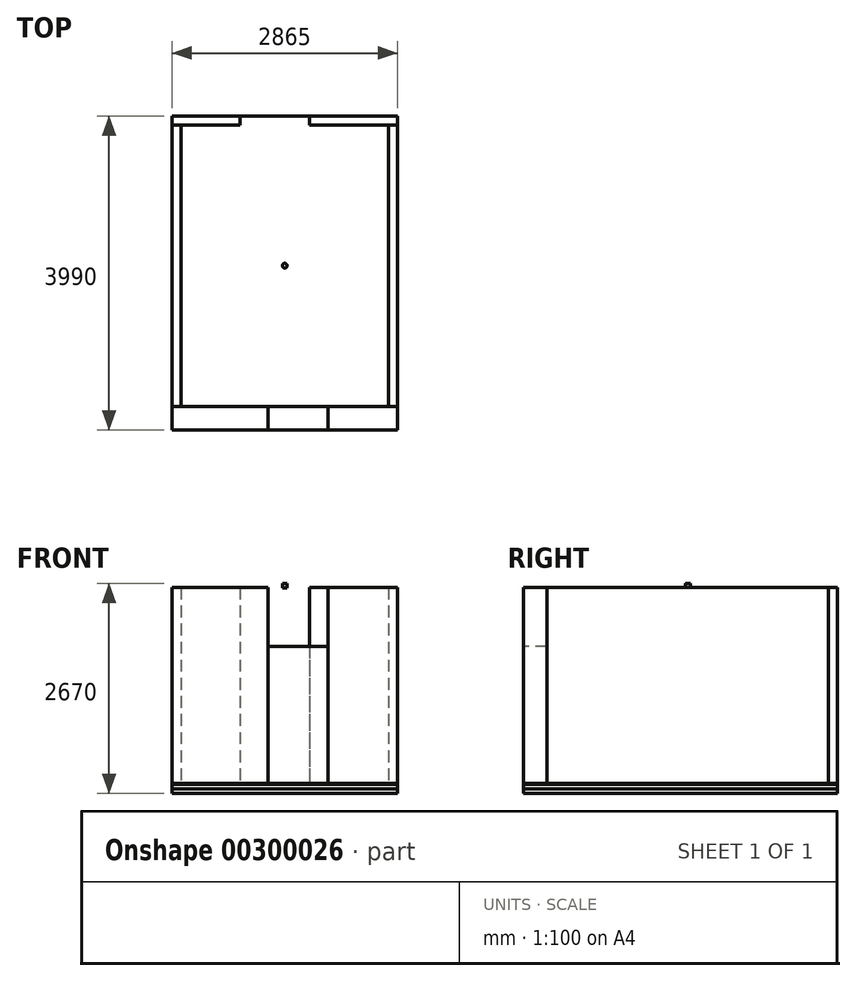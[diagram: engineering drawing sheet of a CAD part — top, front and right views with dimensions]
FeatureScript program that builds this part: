
annotation { "Feature Type Name" : "Feature", "Feature Type Description" : "" }
export const myFeature = defineFeature(function(context is Context, id is Id, definition is map)
    precondition{}
    {
        {
            var Q0;
            Q0=qCreatedBy(makeId("Top.planeOp"),FACE);
            var sketch = newSketch(context, id + "F0", { "sketchPlane" : qUnion([Q0])});
            skLineSegment(sketch, "E0.bottom", {"start": v(1317.5, -1787.5) * mm, "end": v(-1317.5, -1787.5) * mm, "construction": true});
            skLineSegment(sketch, "E0.top", {"start": v(1317.5, 1787.5) * mm, "end": v(-1317.5, 1787.5) * mm, "construction": true});
            skLineSegment(sketch, "E0.left", {"start": v(1317.5, -1787.5) * mm, "end": v(1317.5, 1787.5) * mm, "construction": true});
            skLineSegment(sketch, "E0.right", {"start": v(-1317.5, -1787.5) * mm, "end": v(-1317.5, 1787.5) * mm, "construction": true});
            skPoint(sketch, "E0.middle", {"position": v(0, 0) * mm});
            skLineSegment(sketch, "E1.bottom", {"start": v(-1317.5, 1787.5) * mm, "end": v(-1432.5, 1787.5) * mm});
            skLineSegment(sketch, "E1.top", {"start": v(-1317.5, -1787.5) * mm, "end": v(-1432.5, -1787.5) * mm});
            skLineSegment(sketch, "E1.left", {"start": v(-1317.5, 1787.5) * mm, "end": v(-1317.5, -1787.5) * mm});
            skLineSegment(sketch, "E1.right", {"start": v(-1432.5, 1787.5) * mm, "end": v(-1432.5, -1787.5) * mm});
            skLineSegment(sketch, "E2.bottom", {"start": v(1317.5, -1787.5) * mm, "end": v(1432.5, -1787.5) * mm});
            skLineSegment(sketch, "E2.top", {"start": v(1317.5, 1787.5) * mm, "end": v(1432.5, 1787.5) * mm});
            skLineSegment(sketch, "E2.left", {"start": v(1317.5, -1787.5) * mm, "end": v(1317.5, 1787.5) * mm});
            skLineSegment(sketch, "E2.right", {"start": v(1432.5, -1787.5) * mm, "end": v(1432.5, 1787.5) * mm});
            skLineSegment(sketch, "E3.bottom", {"start": v(-1432.5, -1787.5) * mm, "end": v(-212.5, -1787.5) * mm});
            skLineSegment(sketch, "E3.top", {"start": v(-1432.5, -2087.5) * mm, "end": v(-212.5, -2087.5) * mm});
            skLineSegment(sketch, "E3.left", {"start": v(-1432.5, -1787.5) * mm, "end": v(-1432.5, -2087.5) * mm});
            skLineSegment(sketch, "E3.right", {"start": v(-212.5, -1787.5) * mm, "end": v(-212.5, -2087.5) * mm});
            skLineSegment(sketch, "E4.bottom", {"start": v(1432.5, -1787.5) * mm, "end": v(547.5, -1787.5) * mm});
            skLineSegment(sketch, "E4.top", {"start": v(1432.5, -2087.5) * mm, "end": v(547.5, -2087.5) * mm});
            skLineSegment(sketch, "E4.left", {"start": v(1432.5, -1787.5) * mm, "end": v(1432.5, -2087.5) * mm});
            skLineSegment(sketch, "E4.right", {"start": v(547.5, -1787.5) * mm, "end": v(547.5, -2087.5) * mm});
            skLineSegment(sketch, "E5.bottom", {"start": v(-1432.5, 1787.5) * mm, "end": v(-567.5, 1787.5) * mm});
            skLineSegment(sketch, "E5.top", {"start": v(-1432.5, 1902.5) * mm, "end": v(-567.5, 1902.5) * mm});
            skLineSegment(sketch, "E5.left", {"start": v(-1432.5, 1787.5) * mm, "end": v(-1432.5, 1902.5) * mm});
            skLineSegment(sketch, "E5.right", {"start": v(-567.5, 1787.5) * mm, "end": v(-567.5, 1902.5) * mm});
            skLineSegment(sketch, "E6.bottom", {"start": v(1432.5, 1787.5) * mm, "end": v(317.5, 1787.5) * mm});
            skLineSegment(sketch, "E6.top", {"start": v(1432.5, 1902.5) * mm, "end": v(317.5, 1902.5) * mm});
            skLineSegment(sketch, "E6.left", {"start": v(1432.5, 1787.5) * mm, "end": v(1432.5, 1902.5) * mm});
            skLineSegment(sketch, "E6.right", {"start": v(317.5, 1787.5) * mm, "end": v(317.5, 1902.5) * mm});
            skLineSegment(sketch, "E7.bottom", {"start": v(-212.5, -1787.5) * mm, "end": v(547.5, -1787.5) * mm});
            skLineSegment(sketch, "E7.top", {"start": v(-212.5, -2087.5) * mm, "end": v(547.5, -2087.5) * mm});
            skSolve(sketch);
        }
        {
            var Q0;
            Q0=qCreatedBy(makeId("Top.planeOp"),FACE);
            var sketch = newSketch(context, id + "F1", { "sketchPlane" : qUnion([Q0])});
            skLineSegment(sketch, "E8.bottom", {"start": v(-1432.5, 1902.5) * mm, "end": v(1432.5, 1902.5) * mm});
            skLineSegment(sketch, "E8.top", {"start": v(-1432.5, -2087.5) * mm, "end": v(1432.5, -2087.5) * mm});
            skLineSegment(sketch, "E8.left", {"start": v(-1432.5, 1902.5) * mm, "end": v(-1432.5, -2087.5) * mm});
            skLineSegment(sketch, "E8.right", {"start": v(1432.5, 1902.5) * mm, "end": v(1432.5, -2087.5) * mm});
            skSolve(sketch);
        }
        {
            var Q0;
            Q0 = qSketchRegion(id + "F1", true);
            extrude(context, id + "F2", {"entities" : qUnion([Q0]), "oppositeDirection" : true, "depth" : 15 * mm});
        }
        {
            var Q0;
            Q0=makeQuery(id+"F2.opExtrude","CAP_FACE",FACE,{"disambiguationData":[OSD([sQuery(id+"F1.wireOp",EDGE,"E8.bottom"),sQuery(id+"F1.wireOp",EDGE,"E8.top"),sQuery(id+"F1.wireOp",EDGE,"E8.left"),sQuery(id+"F1.wireOp",EDGE,"E8.right")])],"isStart":false});
            var sketch = newSketch(context, id + "F3", { "sketchPlane" : qUnion([Q0])});
            skLineSegment(sketch, "E9.bottom", {"start": v(1432.5, -1902.5) * mm, "end": v(-1432.5, -1902.5) * mm});
            skLineSegment(sketch, "E9.top", {"start": v(1432.5, 2087.5) * mm, "end": v(-1432.5, 2087.5) * mm});
            skLineSegment(sketch, "E9.left", {"start": v(1432.5, -1902.5) * mm, "end": v(1432.5, 2087.5) * mm});
            skLineSegment(sketch, "E9.right", {"start": v(-1432.5, -1902.5) * mm, "end": v(-1432.5, 2087.5) * mm});
            skSolve(sketch);
        }
        {
            var Q0;
            Q0 = qSketchRegion(id + "F3", true);
            extrude(context, id + "F4", {"entities" : qUnion([Q0]), "depth" : 55 * mm});
        }
        {
            var Q0;
            Q0=makeQuery(id+"F4.opExtrude","CAP_FACE",FACE,{"disambiguationData":[OSD([sQuery(id+"F3.wireOp",EDGE,"E9.bottom"),sQuery(id+"F3.wireOp",EDGE,"E9.top"),sQuery(id+"F3.wireOp",EDGE,"E9.left"),sQuery(id+"F3.wireOp",EDGE,"E9.right")])],"isStart":false});
            var sketch = newSketch(context, id + "F5", { "sketchPlane" : qUnion([Q0])});
            skLineSegment(sketch, "E10.bottom", {"start": v(1432.5, -1902.5) * mm, "end": v(-1432.5, -1902.5) * mm});
            skLineSegment(sketch, "E10.top", {"start": v(1432.5, 2087.5) * mm, "end": v(-1432.5, 2087.5) * mm});
            skLineSegment(sketch, "E10.left", {"start": v(1432.5, -1902.5) * mm, "end": v(1432.5, 2087.5) * mm});
            skLineSegment(sketch, "E10.right", {"start": v(-1432.5, -1902.5) * mm, "end": v(-1432.5, 2087.5) * mm});
            skSolve(sketch);
        }
        {
            var Q0;
            Q0 = qSketchRegion(id + "F5", true);
            extrude(context, id + "F6", {"entities" : qUnion([Q0]), "depth" : 60 * mm});
        }
        {
            assignVariable(context, id + "F7", {"name" : "Wandhoehe", "anyValue" : 2490});
        }
        {
            assignVariable(context, id + "F8", {"name" : "BRHKeller", "anyValue" : 1740});
        }
        {
            var Q0;
            {var subQ0=sQuery(id+"F0.wireOp",EDGE,"E1.left");Q0=makeQuery(id+"F0.imprint","IMPRINT",FACE,{"disambiguationData":[TD([[makeQuery(id+"F0.imprint","IMPRINT",EDGE,{"derivedFrom":subQ0}),-1.0]])]});}
            var Q1;
            {var subQ0=sQuery(id+"F0.wireOp",EDGE,"E2.left");Q1=makeQuery(id+"F0.imprint","IMPRINT",FACE,{"disambiguationData":[TD([[makeQuery(id+"F0.imprint","IMPRINT",EDGE,{"derivedFrom":subQ0}),-1.0]])]});}
            extrude(context, id + "F9", {"entities" : qUnion([Q0, Q1]), "depth" : (getVariable(context, 'Wandhoehe')) * mm});
        }
        {
            var Q0;
            Q0=makeQuery(id+"F0.imprint","IMPRINT",FACE,{"disambiguationData":[TD([[makeQuery(id+"F0.imprint","IMPRINT",EDGE,{"derivedFrom":sQuery(id+"F0.wireOp",EDGE,"E5.top")}),-1.0]])]});
            var Q1;
            Q1=makeQuery(id+"F0.imprint","IMPRINT",FACE,{"disambiguationData":[TD([[makeQuery(id+"F0.imprint","IMPRINT",EDGE,{"derivedFrom":sQuery(id+"F0.wireOp",EDGE,"E6.top")}),1.0]])]});
            extrude(context, id + "F10", {"entities" : qUnion([Q0, Q1]), "depth" : (getVariable(context, 'Wandhoehe')) * mm});
        }
        {
            var Q0;
            Q0=makeQuery(id+"F0.imprint","IMPRINT",FACE,{"disambiguationData":[TD([[makeQuery(id+"F0.imprint","IMPRINT",EDGE,{"derivedFrom":sQuery(id+"F0.wireOp",EDGE,"E3.top")}),1.0]])]});
            var Q1;
            Q1=makeQuery(id+"F0.imprint","IMPRINT",FACE,{"disambiguationData":[TD([[makeQuery(id+"F0.imprint","IMPRINT",EDGE,{"derivedFrom":sQuery(id+"F0.wireOp",EDGE,"E4.top")}),-1.0]])]});
            extrude(context, id + "F11", {"entities" : qUnion([Q0, Q1]), "depth" : (getVariable(context, 'Wandhoehe')) * mm});
        }
        {
            var Q0;
            Q0=makeQuery(id+"F0.imprint","IMPRINT",FACE,{"disambiguationData":[TD([[makeQuery(id+"F0.imprint","IMPRINT",EDGE,{"derivedFrom":sQuery(id+"F0.wireOp",EDGE,"E7.bottom")}),-1.0]])]});
            extrude(context, id + "F12", {"entities" : qUnion([Q0]), "depth" : (getVariable(context, 'BRHKeller')) * mm});
        }
        {
            var Q0;
            Q0=makeQuery(id+"F10.opExtrude","CAP_FACE",FACE,{"disambiguationData":[OSD([sQuery(id+"F0.wireOp",EDGE,"E5.bottom"),sQuery(id+"F0.wireOp",EDGE,"E5.top"),sQuery(id+"F0.wireOp",EDGE,"E5.left"),sQuery(id+"F0.wireOp",EDGE,"E5.right")])],"isStart":false});
            var sketch = newSketch(context, id + "F13", { "sketchPlane" : qUnion([Q0])});
            skLineSegment(sketch, "E11.bottom", {"start": v(-1432.5, 1902.5) * mm, "end": v(1432.5, 1902.5) * mm});
            skLineSegment(sketch, "E11.top", {"start": v(-1432.5, -2087.5) * mm, "end": v(1432.5, -2087.5) * mm});
            skLineSegment(sketch, "E11.left", {"start": v(-1432.5, 1902.5) * mm, "end": v(-1432.5, -2087.5) * mm});
            skLineSegment(sketch, "E11.right", {"start": v(1432.5, 1902.5) * mm, "end": v(1432.5, -2087.5) * mm});
            skSolve(sketch);
        }
        {
            var Q0;
            {var subQ4=makeQuery(id+"F10.opExtrude","CAP_EDGE",EDGE,{"disambiguationData":[OSD([sQuery(id+"F0.wireOp",EDGE,"E5.bottom")])],"isStart":false});Q0=makeQuery(id+"F13.imprint","IMPRINT",FACE,{"disambiguationData":[TD([[makeQuery(id+"F13.imprint","IMPRINT",EDGE,{"derivedFrom":subQ4}),1.0]])]});}
            var sketch = newSketch(context, id + "F14", { "sketchPlane" : qUnion([Q0])});
            skCircle(sketch, "E12", {"center": v(0, 0) * mm, "radius": 30 * mm});
            skSolve(sketch);
        }
        {
            var Q0;
            Q0 = qSketchRegion(id + "F14", true);
            extrude(context, id + "F15", {"entities" : qUnion([Q0]), "depth" : 50 * mm, "hasSecondDirection" : true, "secondDirectionOppositeDirection" : true, "secondDirectionDepth" : 5 * mm});
        }
    });
